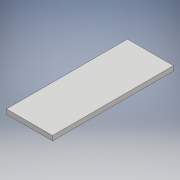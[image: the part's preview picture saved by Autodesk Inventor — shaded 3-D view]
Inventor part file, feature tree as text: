
AUTODESK INVENTOR PART (.ipt)
format: ipt  version: 2018 (Build 220112000, 112)  size: 91,648 bytes
history: native  units: mm
features: other x1, extrude x1
ambient origin geometry x8: Origin, YZ Plane, XZ Plane, XY Plane, X Axis, Y Axis, Z Axis, Center Point
bodies: Body1 (feature_tree)
feature tree (2):
  other  "Sólido1"
  extrude  "Extrusão1"  Depth=125.0mm
